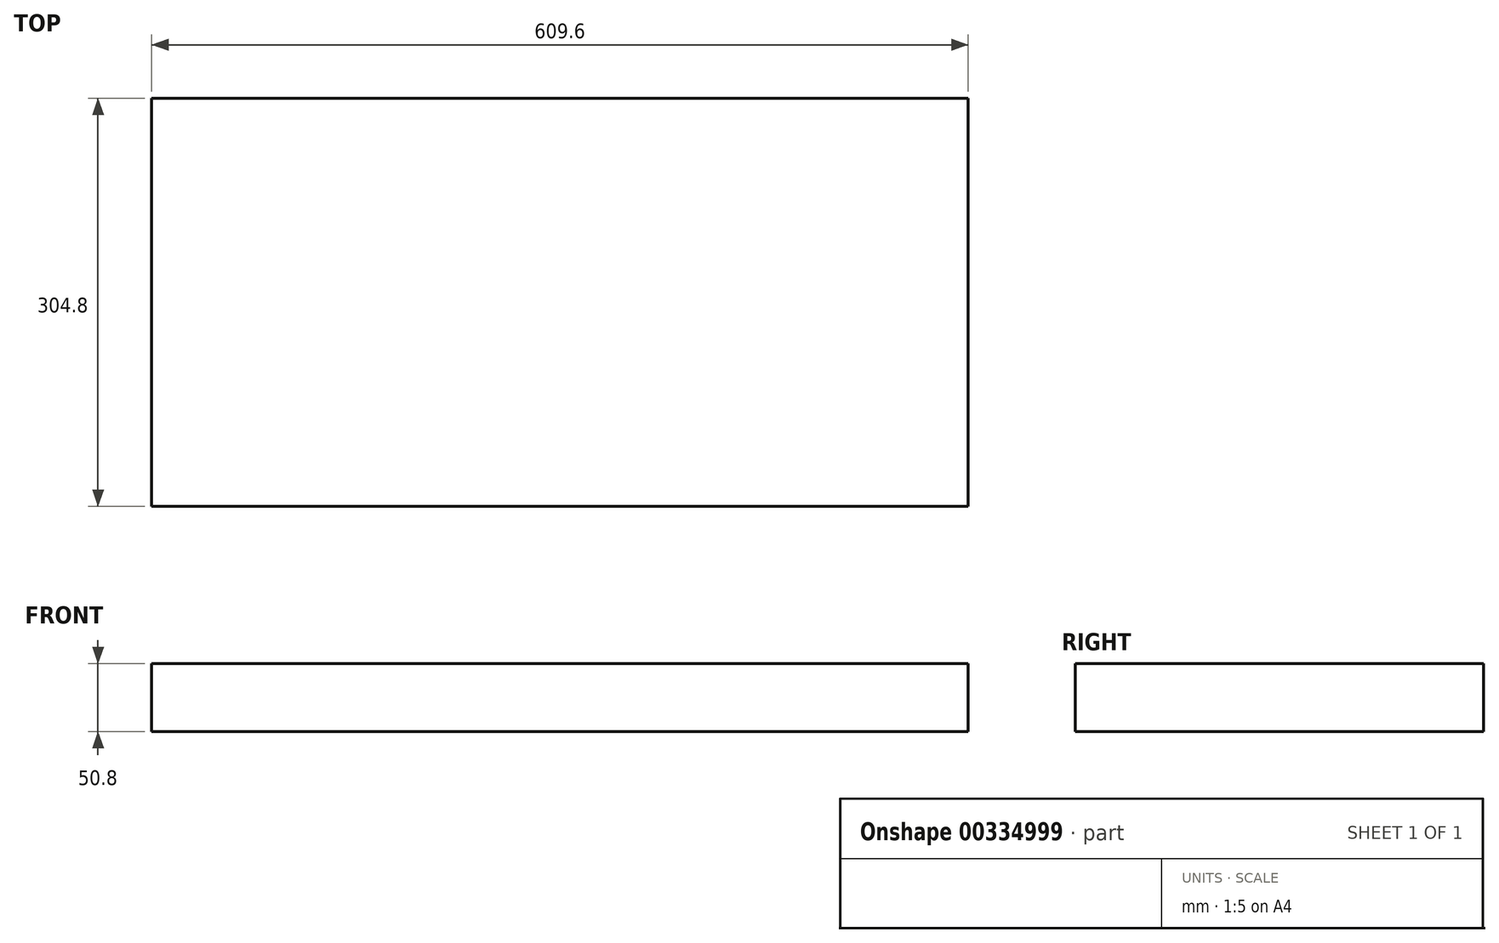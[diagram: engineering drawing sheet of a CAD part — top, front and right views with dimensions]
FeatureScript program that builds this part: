
annotation { "Feature Type Name" : "Feature", "Feature Type Description" : "" }
export const myFeature = defineFeature(function(context is Context, id is Id, definition is map)
    precondition{}
    {
        {
            var Q0;
            Q0=qCreatedBy(makeId("Top.planeOp"),FACE);
            var sketch = newSketch(context, id + "F0", { "sketchPlane" : qUnion([Q0])});
            skLineSegment(sketch, "E0.bottom", {"start": v(-73.43, 255.08) * mm, "end": v(536.17, 255.08) * mm});
            skLineSegment(sketch, "E0.top", {"start": v(-73.43, -49.72) * mm, "end": v(536.17, -49.72) * mm});
            skLineSegment(sketch, "E0.left", {"start": v(-73.43, 255.08) * mm, "end": v(-73.43, -49.72) * mm});
            skLineSegment(sketch, "E0.right", {"start": v(536.17, 255.08) * mm, "end": v(536.17, -49.72) * mm});
            skSolve(sketch);
        }
        {
            var Q0;
            Q0=makeQuery(id+"F0.imprint","IMPRINT",FACE,{"disambiguationData":[TD([[makeQuery(id+"F0.imprint","IMPRINT",EDGE,{"derivedFrom":sQuery(id+"F0.wireOp",EDGE,"E0.bottom")}),-1.0]])]});
            extrude(context, id + "F1", {"entities" : qUnion([Q0]), "oppositeDirection" : true, "depth" : 50.8 * mm});
        }
    });
